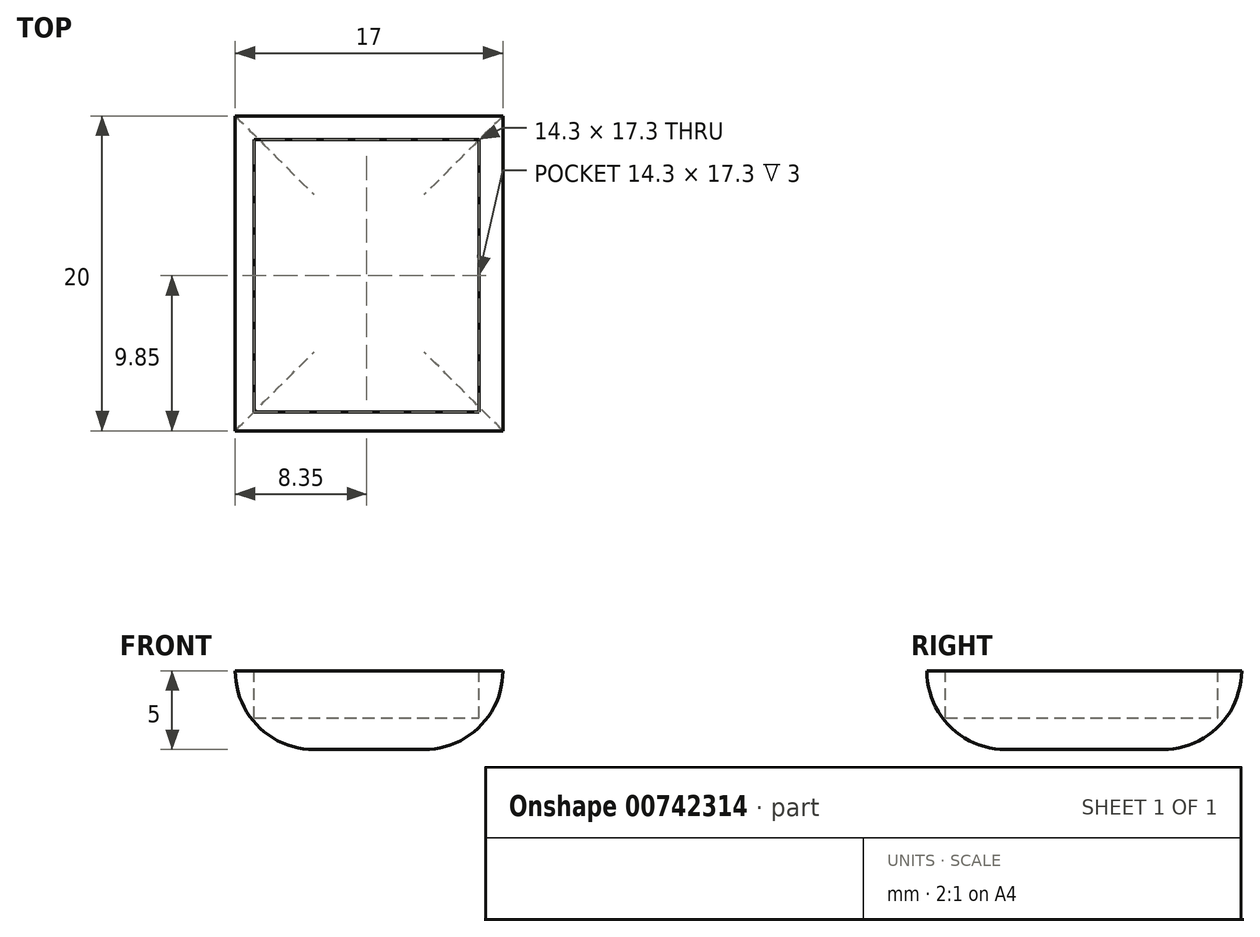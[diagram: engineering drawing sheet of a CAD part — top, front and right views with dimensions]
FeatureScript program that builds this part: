
annotation { "Feature Type Name" : "Feature", "Feature Type Description" : "" }
export const myFeature = defineFeature(function(context is Context, id is Id, definition is map)
    precondition{}
    {
        {
            var Q0;
            Q0=qCreatedBy(makeId("Top.planeOp"),FACE);
            var sketch = newSketch(context, id + "F0", { "sketchPlane" : qUnion([Q0])});
            skLineSegment(sketch, "E0.bottom", {"start": v(0, 0) * mm, "end": v(17, 0) * mm});
            skLineSegment(sketch, "E0.top", {"start": v(0, 20) * mm, "end": v(17, 20) * mm});
            skLineSegment(sketch, "E0.left", {"start": v(0, 0) * mm, "end": v(0, 20) * mm});
            skLineSegment(sketch, "E0.right", {"start": v(17, 0) * mm, "end": v(17, 20) * mm});
            skSolve(sketch);
        }
        {
            var Q0;
            Q0 = qSketchRegion(id + "F0", true);
            extrude(context, id + "F1", {"entities" : qUnion([Q0]), "depth" : 5 * mm, "offsetDistance" : 25 * mm});
        }
        {
            var Q0;
            Q0=makeQuery(id+"F1.opExtrude","CAP_FACE",FACE,{"disambiguationData":[OSD([sQuery(id+"F0.wireOp",EDGE,"E0.bottom"),sQuery(id+"F0.wireOp",EDGE,"E0.top"),sQuery(id+"F0.wireOp",EDGE,"E0.left"),sQuery(id+"F0.wireOp",EDGE,"E0.right")])],"isStart":false});
            var sketch = newSketch(context, id + "F2", { "sketchPlane" : qUnion([Q0])});
            skLineSegment(sketch, "E1.bottom", {"start": v(1.2, 1.2) * mm, "end": v(15.5, 1.2) * mm});
            skLineSegment(sketch, "E1.top", {"start": v(1.2, 18.5) * mm, "end": v(15.5, 18.5) * mm});
            skLineSegment(sketch, "E1.left", {"start": v(1.2, 1.2) * mm, "end": v(1.2, 18.5) * mm});
            skLineSegment(sketch, "E1.right", {"start": v(15.5, 1.2) * mm, "end": v(15.5, 18.5) * mm});
            skSolve(sketch);
        }
        {
            var Q0;
            Q0 = qSketchRegion(id + "F2", true);
            extrude(context, id + "F3", {"entities" : qUnion([Q0]), "operationType" : NewBodyOperationType.REMOVE, "oppositeDirection" : true, "depth" : 3 * mm, "offsetDistance" : 25 * mm});
        }
        {
            var Q0;
            Q0=makeQuery(id+"F1.opExtrude","CAP_EDGE",EDGE,{"disambiguationData":[OSD([sQuery(id+"F0.wireOp",EDGE,"E0.left")])],"isStart":true});
            var Q1;
            Q1=makeQuery(id+"F1.opExtrude","CAP_EDGE",EDGE,{"disambiguationData":[OSD([sQuery(id+"F0.wireOp",EDGE,"E0.top")])],"isStart":true});
            var Q2;
            Q2=makeQuery(id+"F1.opExtrude","CAP_EDGE",EDGE,{"disambiguationData":[OSD([sQuery(id+"F0.wireOp",EDGE,"E0.right")])],"isStart":true});
            var Q3;
            Q3=makeQuery(id+"F1.opExtrude","CAP_EDGE",EDGE,{"disambiguationData":[OSD([sQuery(id+"F0.wireOp",EDGE,"E0.bottom")])],"isStart":true});
            fillet(context, id + "F4", {"entities" : qUnion([Q0, Q1, Q2, Q3]), "radius" : 5 * mm, "tangentPropagation" : true, "allowEdgeOverflow" : false});
        }
    });
